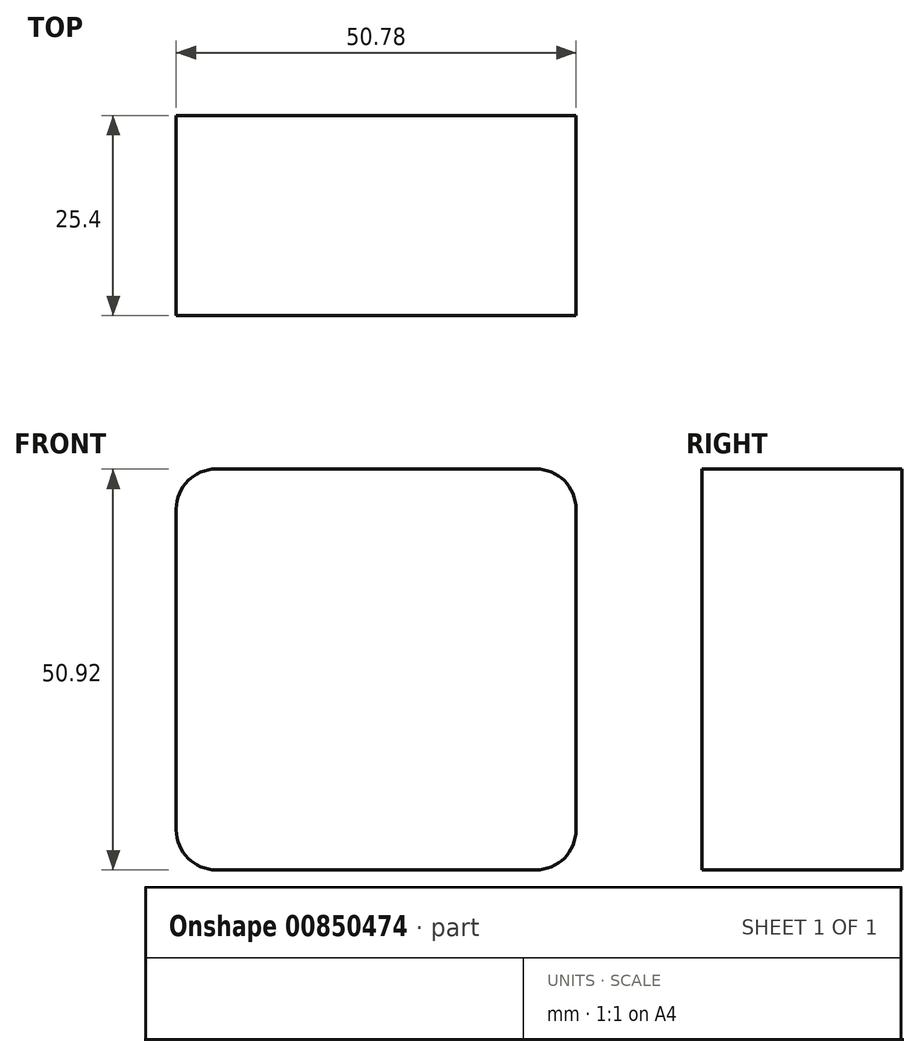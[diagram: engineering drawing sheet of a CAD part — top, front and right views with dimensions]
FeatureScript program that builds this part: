
annotation { "Feature Type Name" : "Feature", "Feature Type Description" : "" }
export const myFeature = defineFeature(function(context is Context, id is Id, definition is map)
    precondition{}
    {
        {
            var Q0;
            Q0=qCreatedBy(makeId("Front.planeOp"),FACE);
            var sketch = newSketch(context, id + "F0", { "sketchPlane" : qUnion([Q0])});
            skLineSegment(sketch, "E0.bottom", {"start": v(-25.39, 25.46) * mm, "end": v(25.39, 25.46) * mm});
            skLineSegment(sketch, "E0.top", {"start": v(-25.39, -25.46) * mm, "end": v(25.39, -25.46) * mm});
            skLineSegment(sketch, "E0.left", {"start": v(-25.39, 25.46) * mm, "end": v(-25.39, -25.46) * mm});
            skLineSegment(sketch, "E0.right", {"start": v(25.39, 25.46) * mm, "end": v(25.39, -25.46) * mm});
            skPoint(sketch, "E0.middle", {"position": v(0, 0) * mm});
            skSolve(sketch);
        }
        {
            var Q0;
            Q0=makeQuery(id+"F0.imprint","IMPRINT",FACE,{"disambiguationData":[TD([[makeQuery(id+"F0.imprint","IMPRINT",EDGE,{"derivedFrom":sQuery(id+"F0.wireOp",EDGE,"E0.bottom")}),-1.0]])]});
            extrude(context, id + "F1", {"entities" : qUnion([Q0]), "depth" : 12.7 * mm, "offsetDistance" : 25.4 * mm});
        }
        {
            var Q0;
            Q0=makeQuery(id+"F1.opExtrude","SWEPT_EDGE",EDGE,{"disambiguationData":[OSD([sQuery(id+"F0.wireOp",EDGE,"E0.bottom"),sQuery(id+"F0.wireOp",EDGE,"E0.right")])]});
            var Q1;
            Q1=makeQuery(id+"F1.opExtrude","SWEPT_EDGE",EDGE,{"disambiguationData":[OSD([sQuery(id+"F0.wireOp",EDGE,"E0.bottom"),sQuery(id+"F0.wireOp",EDGE,"E0.left")])]});
            var Q2;
            Q2=makeQuery(id+"F1.opExtrude","SWEPT_EDGE",EDGE,{"disambiguationData":[OSD([sQuery(id+"F0.wireOp",EDGE,"E0.top"),sQuery(id+"F0.wireOp",EDGE,"E0.left")])]});
            var Q3;
            Q3=makeQuery(id+"F1.opExtrude","SWEPT_EDGE",EDGE,{"disambiguationData":[OSD([sQuery(id+"F0.wireOp",EDGE,"E0.top"),sQuery(id+"F0.wireOp",EDGE,"E0.right")])]});
            fillet(context, id + "F2", {"entities" : qUnion([Q0, Q1, Q2, Q3]), "radius" : 5.08 * mm, "tangentPropagation" : true, "allowEdgeOverflow" : false});
        }
        {
            var Q0;
            Q0=makeQuery(id+"F0.imprint","IMPRINT",FACE,{"disambiguationData":[TD([[makeQuery(id+"F0.imprint","IMPRINT",EDGE,{"derivedFrom":sQuery(id+"F0.wireOp",EDGE,"E0.bottom")}),-1.0]])]});
            extrude(context, id + "F3", {"entities" : qUnion([Q0]), "operationType" : NewBodyOperationType.ADD, "oppositeDirection" : true, "depth" : 12.7 * mm, "offsetDistance" : 25.4 * mm});
        }
        {
            var Q0;
            Q0=makeQuery(id+"F3.opExtrude","SWEPT_EDGE",EDGE,{"disambiguationData":[OSD([sQuery(id+"F0.wireOp",EDGE,"E0.bottom"),sQuery(id+"F0.wireOp",EDGE,"E0.left")])]});
            var Q1;
            Q1=makeQuery(id+"F3.opExtrude","SWEPT_EDGE",EDGE,{"disambiguationData":[OSD([sQuery(id+"F0.wireOp",EDGE,"E0.top"),sQuery(id+"F0.wireOp",EDGE,"E0.left")])]});
            var Q2;
            Q2=makeQuery(id+"F3.opExtrude","SWEPT_EDGE",EDGE,{"disambiguationData":[OSD([sQuery(id+"F0.wireOp",EDGE,"E0.top"),sQuery(id+"F0.wireOp",EDGE,"E0.right")])]});
            var Q3;
            Q3=makeQuery(id+"F3.opExtrude","SWEPT_EDGE",EDGE,{"disambiguationData":[OSD([sQuery(id+"F0.wireOp",EDGE,"E0.bottom"),sQuery(id+"F0.wireOp",EDGE,"E0.right")])]});
            fillet(context, id + "F4", {"entities" : qUnion([Q0, Q1, Q2, Q3]), "radius" : 5.08 * mm, "tangentPropagation" : true, "allowEdgeOverflow" : false});
        }
    });
